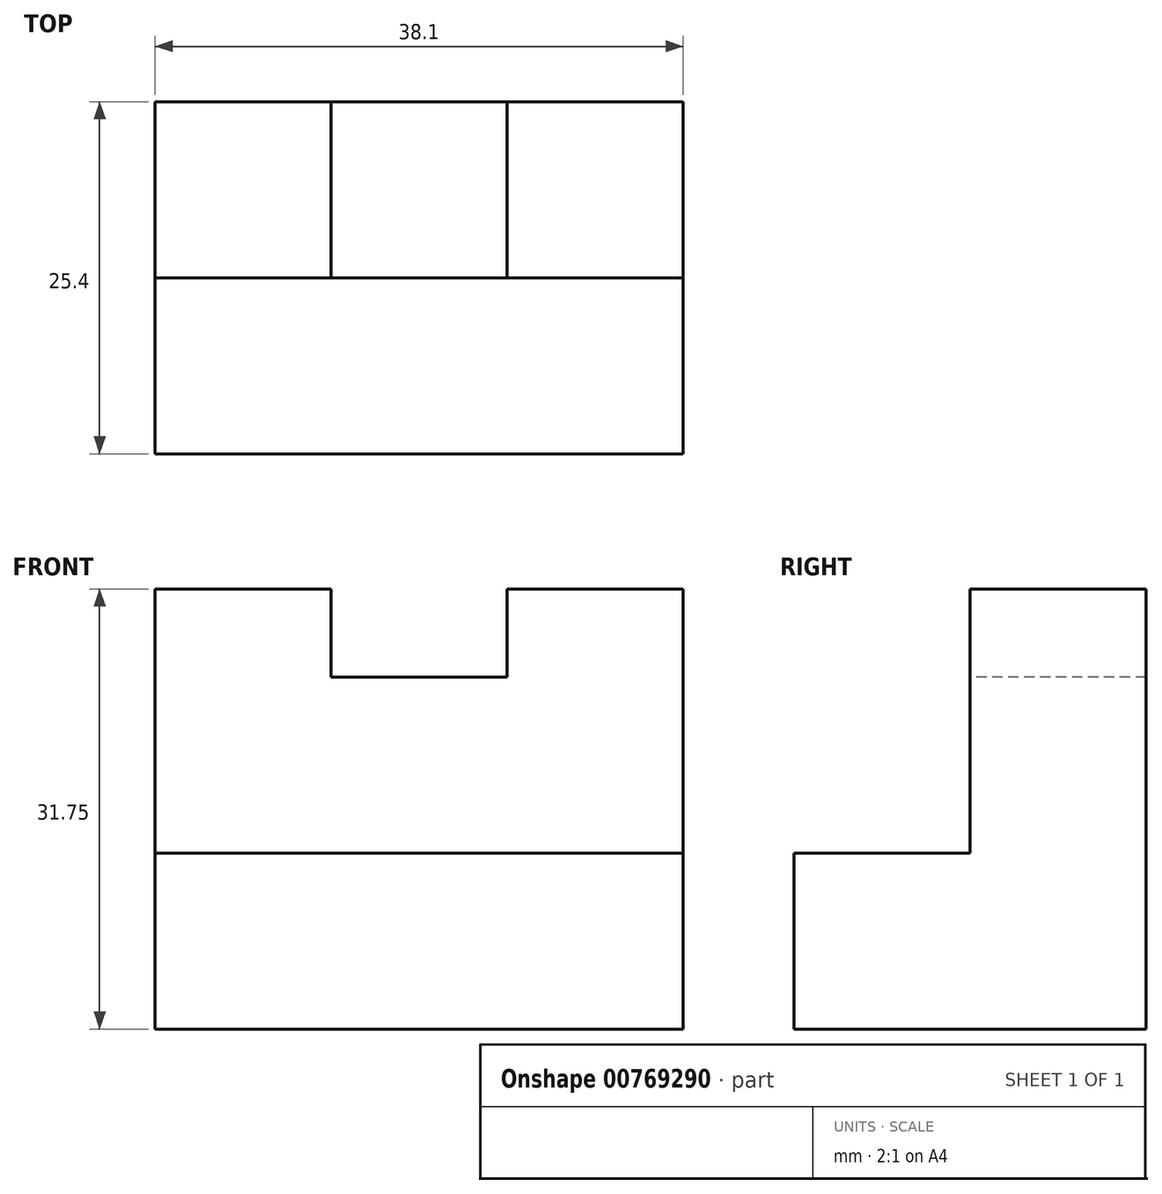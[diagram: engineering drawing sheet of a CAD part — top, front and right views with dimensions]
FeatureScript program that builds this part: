
annotation { "Feature Type Name" : "Feature", "Feature Type Description" : "" }
export const myFeature = defineFeature(function(context is Context, id is Id, definition is map)
    precondition{}
    {
        {
            var Q0;
            Q0=qCreatedBy(makeId("Front.planeOp"),FACE);
            var sketch = newSketch(context, id + "F0", { "sketchPlane" : qUnion([Q0])});
            skLineSegment(sketch, "E0", {"start": v(0, 0) * mm, "end": v(38.1, 0) * mm});
            skLineSegment(sketch, "E1", {"start": v(0, 0) * mm, "end": v(0, 31.75) * mm});
            skLineSegment(sketch, "E2", {"start": v(0, 31.75) * mm, "end": v(38.1, 31.75) * mm});
            skLineSegment(sketch, "E3", {"start": v(38.1, 31.75) * mm, "end": v(38.1, 0) * mm});
            skSolve(sketch);
        }
        {
            var Q0;
            Q0 = qSketchRegion(id + "F0", true);
            extrude(context, id + "F1", {"entities" : qUnion([Q0]), "depth" : 25.4 * mm, "offsetDistance" : 25.4 * mm});
        }
        {
            var Q0;
            Q0=makeQuery(id+"F1.opExtrude","CAP_FACE",FACE,{"disambiguationData":[OSD([sQuery(id+"F0.wireOp",EDGE,"E0"),sQuery(id+"F0.wireOp",EDGE,"E1"),sQuery(id+"F0.wireOp",EDGE,"E2"),sQuery(id+"F0.wireOp",EDGE,"E3")])],"isStart":false});
            var sketch = newSketch(context, id + "F2", { "sketchPlane" : qUnion([Q0])});
            skLineSegment(sketch, "E4", {"start": v(0, 0) * mm, "end": v(0, 12.7) * mm});
            skLineSegment(sketch, "E5", {"start": v(0, 12.7) * mm, "end": v(38.1, 12.7) * mm});
            skLineSegment(sketch, "E6", {"start": v(38.1, 12.7) * mm, "end": v(38.1, 0) * mm});
            skLineSegment(sketch, "E7", {"start": v(38.1, 0) * mm, "end": v(0, 0) * mm});
            skSolve(sketch);
        }
        {
            var Q0;
            {var subQ0=sQuery(id+"F2.wireOp",EDGE,"E5");Q0=makeQuery(id+"F2.imprint","IMPRINT",FACE,{"disambiguationData":[TD([[makeQuery(id+"F2.imprint","IMPRINT",EDGE,{"derivedFrom":subQ0}),1.0]])]});}
            extrude(context, id + "F3", {"entities" : qUnion([Q0]), "operationType" : NewBodyOperationType.REMOVE, "oppositeDirection" : true, "depth" : 12.7 * mm, "offsetDistance" : 25.4 * mm});
        }
        {
            var Q0;
            Q0=makeQuery(id+"F3.boolean.opBoolean","COPY",FACE,{"derivedFrom":makeQuery(id+"F3.opExtrude","CAP_FACE",FACE,{"disambiguationData":[OSD([sQuery(id+"F0.wireOp",EDGE,"E1"),sQuery(id+"F0.wireOp",EDGE,"E2"),sQuery(id+"F0.wireOp",EDGE,"E3"),sQuery(id+"F2.wireOp",EDGE,"E5")])],"isStart":false})});
            var sketch = newSketch(context, id + "F4", { "sketchPlane" : qUnion([Q0])});
            skLineSegment(sketch, "E8", {"start": v(0, 31.75) * mm, "end": v(12.7, 31.75) * mm});
            skLineSegment(sketch, "E9", {"start": v(38.1, 31.75) * mm, "end": v(25.4, 31.75) * mm});
            skLineSegment(sketch, "E10", {"start": v(12.7, 31.75) * mm, "end": v(12.7, 25.4) * mm});
            skLineSegment(sketch, "E11", {"start": v(12.7, 25.4) * mm, "end": v(25.4, 25.4) * mm});
            skLineSegment(sketch, "E12", {"start": v(25.4, 31.75) * mm, "end": v(25.4, 25.4) * mm});
            skSolve(sketch);
        }
        {
            var Q0;
            {var subQ0=sQuery(id+"F4.wireOp",EDGE,"E10");Q0=makeQuery(id+"F4.imprint","IMPRINT",FACE,{"disambiguationData":[TD([[makeQuery(id+"F4.imprint","IMPRINT",EDGE,{"derivedFrom":subQ0}),1.0]])]});}
            extrude(context, id + "F5", {"entities" : qUnion([Q0]), "operationType" : NewBodyOperationType.REMOVE, "oppositeDirection" : true, "depth" : 12.7 * mm, "offsetDistance" : 25.4 * mm});
        }
    });
